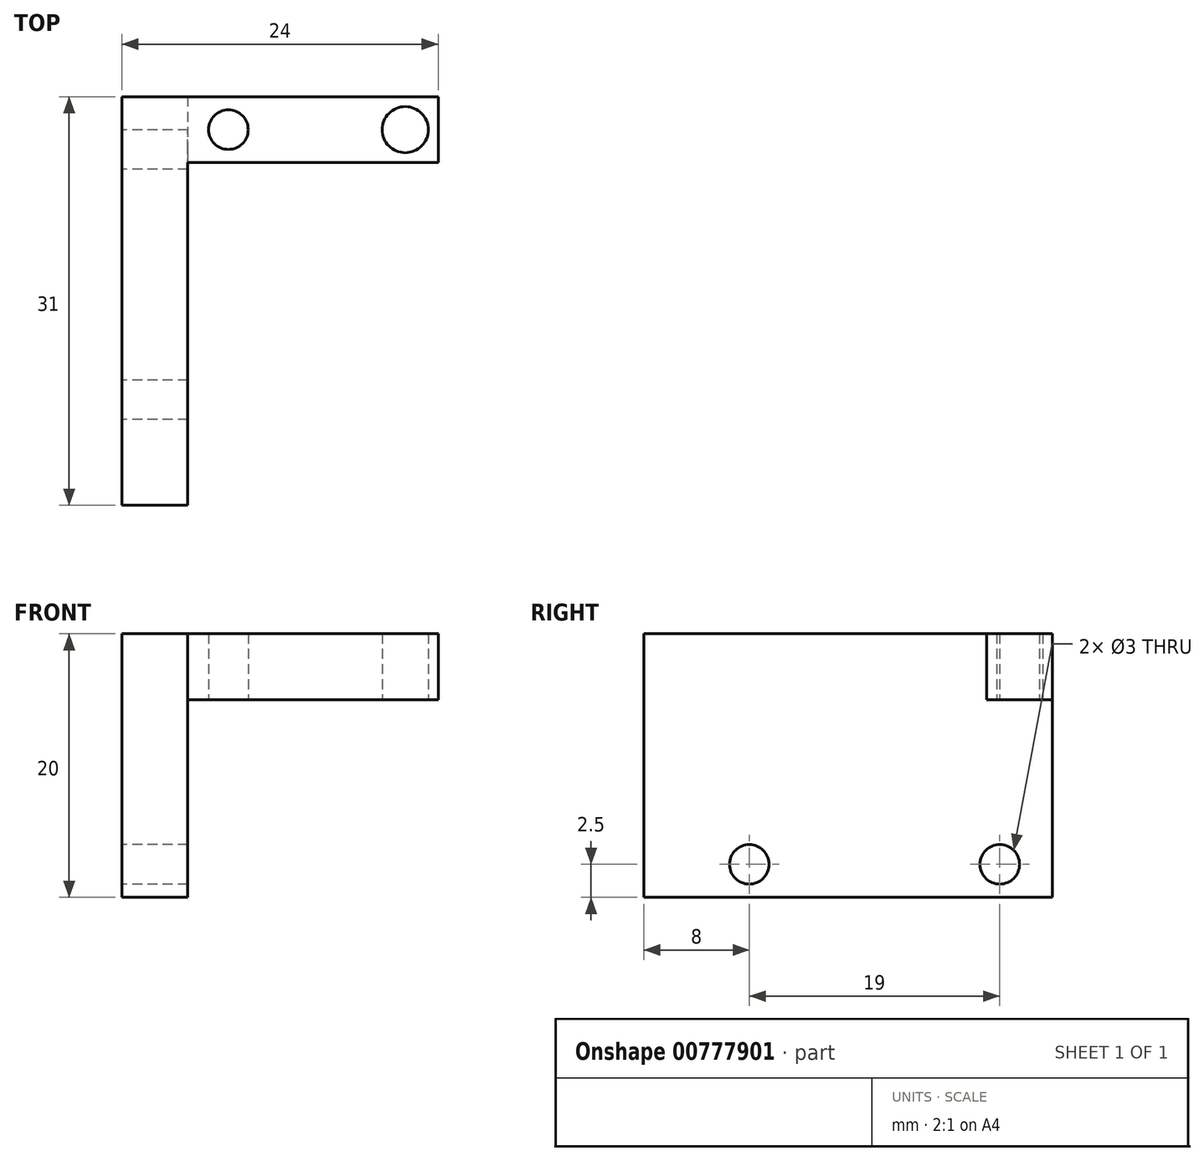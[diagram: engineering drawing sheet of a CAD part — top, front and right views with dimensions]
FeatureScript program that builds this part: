
annotation { "Feature Type Name" : "Feature", "Feature Type Description" : "" }
export const myFeature = defineFeature(function(context is Context, id is Id, definition is map)
    precondition{}
    {
        {
            var Q0;
            Q0=qCreatedBy(makeId("Top.planeOp"),FACE);
            var sketch = newSketch(context, id + "F0", { "sketchPlane" : qUnion([Q0])});
            skLineSegment(sketch, "E0", {"start": v(0, 0) * mm, "end": v(24, 0) * mm});
            skLineSegment(sketch, "E1", {"start": v(24, 0) * mm, "end": v(24, -5) * mm});
            skLineSegment(sketch, "E2", {"start": v(24, -5) * mm, "end": v(5, -5) * mm});
            skLineSegment(sketch, "E3", {"start": v(5, -5) * mm, "end": v(5, -31) * mm});
            skLineSegment(sketch, "E4", {"start": v(5, -31) * mm, "end": v(0, -31) * mm});
            skLineSegment(sketch, "E5", {"start": v(0, -31) * mm, "end": v(0, 0) * mm});
            skPoint(sketch, "E6.centerSnap0", {"position": v(24, -2.5) * mm});
            skCircle(sketch, "E7", {"center": v(8.09, -2.5) * mm, "radius": 1.5 * mm});
            skPoint(sketch, "E8", {"position": v(21.5, -2.5) * mm});
            skSolve(sketch);
        }
        {
            var Q0;
            Q0 = qSketchRegion(id + "F0", true);
            extrude(context, id + "F1", {"entities" : qUnion([Q0]), "depth" : 5 * mm, "offsetDistance" : 25 * mm});
        }
        {
            var Q0;
            Q0=qCreatedBy(makeId("Top.planeOp"),FACE);
            var sketch = newSketch(context, id + "F2", { "sketchPlane" : qUnion([Q0])});
            skPoint(sketch, "E9.0", {"position": v(21.5, -2.5) * mm});
            skCircle(sketch, "E10", {"center": v(21.5, -2.5) * mm, "radius": 1.75 * mm});
            skSolve(sketch);
        }
        {
            var Q0;
            Q0=makeQuery(id+"F1.opExtrude","CAP_FACE",FACE,{"disambiguationData":[OSD([sQuery(id+"F0.wireOp",EDGE,"E0"),sQuery(id+"F0.wireOp",EDGE,"E1"),sQuery(id+"F0.wireOp",EDGE,"E2"),sQuery(id+"F0.wireOp",EDGE,"E3"),sQuery(id+"F0.wireOp",EDGE,"E4"),sQuery(id+"F0.wireOp",EDGE,"E5"),sQuery(id+"F0.wireOp",EDGE,"E6")])],"isStart":false});
            var sketch = newSketch(context, id + "F3", { "sketchPlane" : qUnion([Q0])});
            skLineSegment(sketch, "E11.bottom", {"start": v(0, 0) * mm, "end": v(5, 0) * mm});
            skLineSegment(sketch, "E11.top", {"start": v(0, -31) * mm, "end": v(5, -31) * mm});
            skLineSegment(sketch, "E11.left", {"start": v(0, 0) * mm, "end": v(0, -31) * mm});
            skLineSegment(sketch, "E11.right", {"start": v(5, 0) * mm, "end": v(5, -31) * mm});
            skSolve(sketch);
        }
        {
            var Q0;
            Q0 = qSketchRegion(id + "F2", true);
            extrude(context, id + "F4", {"entities" : qUnion([Q0]), "operationType" : NewBodyOperationType.REMOVE, "depth" : 7 * mm, "offsetDistance" : 25 * mm});
        }
        {
            var Q0;
            Q0 = qSketchRegion(id + "F3", true);
            extrude(context, id + "F5", {"entities" : qUnion([Q0]), "operationType" : NewBodyOperationType.ADD, "oppositeDirection" : true, "depth" : 20 * mm, "offsetDistance" : 25 * mm});
        }
        {
            var Q0;
            Q0=makeQuery(id+"F1.opExtrude","SWEPT_FACE",FACE,{"disambiguationData":[OSD([sQuery(id+"F0.wireOp",EDGE,"E5")])]});
            var sketch = newSketch(context, id + "F6", { "sketchPlane" : qUnion([Q0])});
            skCircle(sketch, "E12", {"center": v(23, -12.5) * mm, "radius": 1.5 * mm});
            skPoint(sketch, "E12.centerSnap0", {"position": v(31, -12.5) * mm});
            skCircle(sketch, "E13", {"center": v(4, -12.5) * mm, "radius": 1.5 * mm});
            skSolve(sketch);
        }
        {
            var Q0;
            Q0 = qSketchRegion(id + "F6", true);
            extrude(context, id + "F7", {"entities" : qUnion([Q0]), "operationType" : NewBodyOperationType.REMOVE, "oppositeDirection" : true, "depth" : 25 * mm, "offsetDistance" : 25 * mm});
        }
    });
